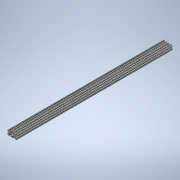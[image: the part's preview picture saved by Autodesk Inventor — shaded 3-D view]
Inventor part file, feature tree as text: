
AUTODESK INVENTOR PART (.ipt)
format: ipt  version: 2020 (Build 240168000, 168)  size: 340,992 bytes
history: native  units: in
note: dims shown in document units (in); Inventor stores cm internally (conversion verified against a paired STEP export)
features: sketch x2, extrude x1
ambient origin geometry x8: Origin, YZ Plane, XZ Plane, XY Plane, X Axis, Y Axis, Z Axis, Center Point
bodies: Solid1 (feature_tree)
feature tree (3):
  extrude  "Extrusion1"  [1 undecoded]
  sketch  "Sketch2"
  sketch  "Sketch1"  dims[d0=34.0in d1=0.0in]
note: 1 required parameter value undecoded (feature->parameter linkage not recoverable at this tier; creation-order binding heuristic only, values carry confidence <= 0.55)
